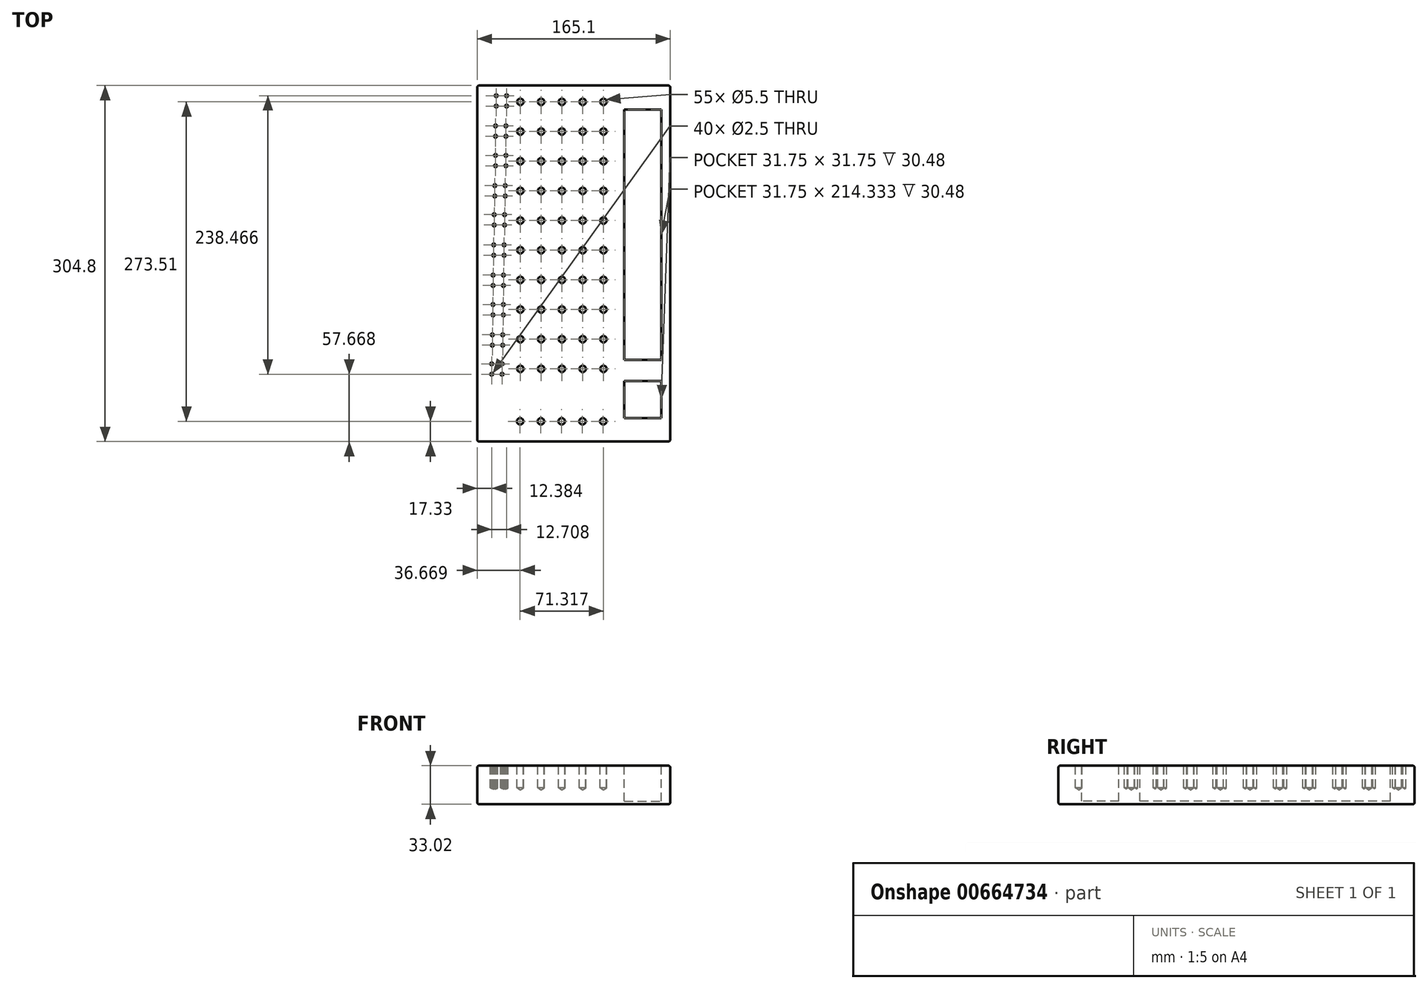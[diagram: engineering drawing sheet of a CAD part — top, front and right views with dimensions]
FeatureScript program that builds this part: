
annotation { "Feature Type Name" : "Feature", "Feature Type Description" : "" }
export const myFeature = defineFeature(function(context is Context, id is Id, definition is map)
    precondition{}
    {
        {
            var Q0;
            Q0=qCreatedBy(makeId("Top.planeOp"),FACE);
            var sketch = newSketch(context, id + "F0", { "sketchPlane" : qUnion([Q0])});
            skLineSegment(sketch, "E0.bottom", {"start": v(-165.1, 224.78) * mm, "end": v(0, 224.78) * mm});
            skLineSegment(sketch, "E0.top", {"start": v(-165.1, -80.02) * mm, "end": v(0, -80.02) * mm});
            skLineSegment(sketch, "E0.left", {"start": v(-165.1, 224.78) * mm, "end": v(-165.1, -80.02) * mm});
            skLineSegment(sketch, "E0.right", {"start": v(0, 224.78) * mm, "end": v(0, -80.02) * mm});
            skSolve(sketch);
        }
        {
            var Q0;
            Q0=makeQuery(id+"F0.imprint","IMPRINT",FACE,{"disambiguationData":[TD([[makeQuery(id+"F0.imprint","IMPRINT",EDGE,{"derivedFrom":sQuery(id+"F0.wireOp",EDGE,"E0.bottom")}),-1.0]])]});
            extrude(context, id + "F1", {"entities" : qUnion([Q0]), "oppositeDirection" : true, "depth" : 33.02 * mm, "offsetDistance" : 25.4 * mm});
        }
        {
            var Q0;
            Q0=makeQuery(id+"F1.opExtrude","SWEPT_FACE",FACE,{"disambiguationData":[OSD([sQuery(id+"F0.wireOp",EDGE,"E0.right")])]});
            var Q1;
            Q1=makeQuery(id+"F1.opExtrude","SWEPT_FACE",FACE,{"disambiguationData":[OSD([sQuery(id+"F0.wireOp",EDGE,"E0.top")])]});
            var Q2;
            Q2=makeQuery(id+"F1.opExtrude","SWEPT_FACE",FACE,{"disambiguationData":[OSD([sQuery(id+"F0.wireOp",EDGE,"E0.left")])]});
            var Q3;
            Q3=makeQuery(id+"F1.opExtrude","SWEPT_FACE",FACE,{"disambiguationData":[OSD([sQuery(id+"F0.wireOp",EDGE,"E0.bottom")])]});
            fillet(context, id + "F2", {"entities" : qUnion([Q0, Q1, Q2, Q3]), "radius" : 1.59 * mm, "tangentPropagation" : true, "allowEdgeOverflow" : false});
        }
        {
            var Q0;
            Q0=makeQuery(id+"F1.opExtrude","CAP_FACE",FACE,{"disambiguationData":[OSD([sQuery(id+"F0.wireOp",EDGE,"E0.bottom"),sQuery(id+"F0.wireOp",EDGE,"E0.top"),sQuery(id+"F0.wireOp",EDGE,"E0.left"),sQuery(id+"F0.wireOp",EDGE,"E0.right")])],"isStart":true});
            var sketch = newSketch(context, id + "F3", { "sketchPlane" : qUnion([Q0])});
            skCircle(sketch, "E1", {"center": v(-128.23, -17.78) * mm, "radius": 2.75 * mm});
            skCircle(sketch, "E2.0.1.0", {"center": v(-128.23, 7.62) * mm, "radius": 2.75 * mm});
            skCircle(sketch, "E2.0.2.0", {"center": v(-128.23, 33.02) * mm, "radius": 2.75 * mm});
            skCircle(sketch, "E2.0.3.0", {"center": v(-128.23, 58.42) * mm, "radius": 2.75 * mm});
            skCircle(sketch, "E2.0.4.0", {"center": v(-128.23, 83.82) * mm, "radius": 2.75 * mm});
            skCircle(sketch, "E2.0.5.0", {"center": v(-128.23, 109.22) * mm, "radius": 2.75 * mm});
            skCircle(sketch, "E2.0.6.0", {"center": v(-128.23, 134.62) * mm, "radius": 2.75 * mm});
            skCircle(sketch, "E2.0.7.0", {"center": v(-128.23, 160.02) * mm, "radius": 2.75 * mm});
            skCircle(sketch, "E2.0.8.0", {"center": v(-128.23, 185.42) * mm, "radius": 2.75 * mm});
            skCircle(sketch, "E2.0.9.0", {"center": v(-128.23, 210.82) * mm, "radius": 2.75 * mm});
            skCircle(sketch, "E2.1.0.0", {"center": v(-110.45, -17.78) * mm, "radius": 2.75 * mm});
            skCircle(sketch, "E2.1.1.0", {"center": v(-110.45, 7.62) * mm, "radius": 2.75 * mm});
            skCircle(sketch, "E2.1.2.0", {"center": v(-110.45, 33.02) * mm, "radius": 2.75 * mm});
            skCircle(sketch, "E2.1.3.0", {"center": v(-110.45, 58.42) * mm, "radius": 2.75 * mm});
            skCircle(sketch, "E2.1.4.0", {"center": v(-110.45, 83.82) * mm, "radius": 2.75 * mm});
            skCircle(sketch, "E2.1.5.0", {"center": v(-110.45, 109.22) * mm, "radius": 2.75 * mm});
            skCircle(sketch, "E2.1.6.0", {"center": v(-110.45, 134.62) * mm, "radius": 2.75 * mm});
            skCircle(sketch, "E2.1.7.0", {"center": v(-110.45, 160.02) * mm, "radius": 2.75 * mm});
            skCircle(sketch, "E2.1.8.0", {"center": v(-110.45, 185.42) * mm, "radius": 2.75 * mm});
            skCircle(sketch, "E2.1.9.0", {"center": v(-110.45, 210.82) * mm, "radius": 2.75 * mm});
            skCircle(sketch, "E2.2.0.0", {"center": v(-92.67, -17.78) * mm, "radius": 2.75 * mm});
            skCircle(sketch, "E2.2.1.0", {"center": v(-92.67, 7.62) * mm, "radius": 2.75 * mm});
            skCircle(sketch, "E2.2.2.0", {"center": v(-92.67, 33.02) * mm, "radius": 2.75 * mm});
            skCircle(sketch, "E2.2.3.0", {"center": v(-92.67, 58.42) * mm, "radius": 2.75 * mm});
            skCircle(sketch, "E2.2.4.0", {"center": v(-92.67, 83.82) * mm, "radius": 2.75 * mm});
            skCircle(sketch, "E2.2.5.0", {"center": v(-92.67, 109.22) * mm, "radius": 2.75 * mm});
            skCircle(sketch, "E2.2.6.0", {"center": v(-92.67, 134.62) * mm, "radius": 2.75 * mm});
            skCircle(sketch, "E2.2.7.0", {"center": v(-92.67, 160.02) * mm, "radius": 2.75 * mm});
            skCircle(sketch, "E2.2.8.0", {"center": v(-92.67, 185.42) * mm, "radius": 2.75 * mm});
            skCircle(sketch, "E2.2.9.0", {"center": v(-92.67, 210.82) * mm, "radius": 2.75 * mm});
            skCircle(sketch, "E2.3.0.0", {"center": v(-74.9, -17.78) * mm, "radius": 2.75 * mm});
            skCircle(sketch, "E2.3.1.0", {"center": v(-74.9, 7.62) * mm, "radius": 2.75 * mm});
            skCircle(sketch, "E2.3.2.0", {"center": v(-74.9, 33.02) * mm, "radius": 2.75 * mm});
            skCircle(sketch, "E2.3.3.0", {"center": v(-74.9, 58.42) * mm, "radius": 2.75 * mm});
            skCircle(sketch, "E2.3.4.0", {"center": v(-74.9, 83.82) * mm, "radius": 2.75 * mm});
            skCircle(sketch, "E2.3.5.0", {"center": v(-74.9, 109.22) * mm, "radius": 2.75 * mm});
            skCircle(sketch, "E2.3.6.0", {"center": v(-74.9, 134.62) * mm, "radius": 2.75 * mm});
            skCircle(sketch, "E2.3.7.0", {"center": v(-74.9, 160.02) * mm, "radius": 2.75 * mm});
            skCircle(sketch, "E2.3.8.0", {"center": v(-74.9, 185.42) * mm, "radius": 2.75 * mm});
            skCircle(sketch, "E2.3.9.0", {"center": v(-74.9, 210.82) * mm, "radius": 2.75 * mm});
            skCircle(sketch, "E2.4.0.0", {"center": v(-57.11, -17.78) * mm, "radius": 2.75 * mm});
            skCircle(sketch, "E2.4.1.0", {"center": v(-57.11, 7.62) * mm, "radius": 2.75 * mm});
            skCircle(sketch, "E2.4.2.0", {"center": v(-57.11, 33.02) * mm, "radius": 2.75 * mm});
            skCircle(sketch, "E2.4.3.0", {"center": v(-57.11, 58.42) * mm, "radius": 2.75 * mm});
            skCircle(sketch, "E2.4.4.0", {"center": v(-57.11, 83.82) * mm, "radius": 2.75 * mm});
            skCircle(sketch, "E2.4.5.0", {"center": v(-57.11, 109.22) * mm, "radius": 2.75 * mm});
            skCircle(sketch, "E2.4.6.0", {"center": v(-57.11, 134.62) * mm, "radius": 2.75 * mm});
            skCircle(sketch, "E2.4.7.0", {"center": v(-57.11, 160.02) * mm, "radius": 2.75 * mm});
            skCircle(sketch, "E2.4.8.0", {"center": v(-57.11, 185.42) * mm, "radius": 2.75 * mm});
            skCircle(sketch, "E2.4.9.0", {"center": v(-57.11, 210.82) * mm, "radius": 2.75 * mm});
            skLineSegment(sketch, "E2.direction1", {"start": v(-128.23, -17.78) * mm, "end": v(-110.45, -17.78) * mm, "construction": true});
            skLineSegment(sketch, "E2.direction2", {"start": v(-128.23, -17.78) * mm, "end": v(-128.23, 7.62) * mm, "construction": true});
            skCircle(sketch, "E3", {"center": v(-148.9, 207.22) * mm, "radius": 1.27 * mm});
            skCircle(sketch, "E4.0.1.0", {"center": v(-148.9, 216.11) * mm, "radius": 1.27 * mm});
            skCircle(sketch, "E4.1.0.0", {"center": v(-140, 207.22) * mm, "radius": 1.27 * mm});
            skCircle(sketch, "E4.1.1.0", {"center": v(-140, 216.11) * mm, "radius": 1.27 * mm});
            skLineSegment(sketch, "E4.direction1", {"start": v(-148.9, 207.22) * mm, "end": v(-140, 207.22) * mm, "construction": true});
            skLineSegment(sketch, "E4.direction2", {"start": v(-148.9, 207.22) * mm, "end": v(-148.9, 216.11) * mm, "construction": true});
            skCircle(sketch, "E5", {"center": v(-149.45, 181.36) * mm, "radius": 1.27 * mm});
            skCircle(sketch, "E6.0.1.0", {"center": v(-149.45, 190.25) * mm, "radius": 1.27 * mm});
            skCircle(sketch, "E6.1.0.0", {"center": v(-140.56, 181.36) * mm, "radius": 1.27 * mm});
            skCircle(sketch, "E6.1.1.0", {"center": v(-140.56, 190.25) * mm, "radius": 1.27 * mm});
            skLineSegment(sketch, "E6.direction1", {"start": v(-149.45, 181.36) * mm, "end": v(-140.56, 181.36) * mm, "construction": true});
            skLineSegment(sketch, "E6.direction2", {"start": v(-149.45, 181.36) * mm, "end": v(-149.45, 190.25) * mm, "construction": true});
            skCircle(sketch, "E7", {"center": v(-149.51, 156.12) * mm, "radius": 1.27 * mm});
            skCircle(sketch, "E8.0.1.0", {"center": v(-149.51, 165) * mm, "radius": 1.27 * mm});
            skCircle(sketch, "E8.1.0.0", {"center": v(-140.62, 156.12) * mm, "radius": 1.27 * mm});
            skCircle(sketch, "E8.1.1.0", {"center": v(-140.62, 165) * mm, "radius": 1.27 * mm});
            skLineSegment(sketch, "E8.direction1", {"start": v(-149.51, 156.12) * mm, "end": v(-140.62, 156.12) * mm, "construction": true});
            skLineSegment(sketch, "E8.direction2", {"start": v(-149.51, 156.12) * mm, "end": v(-149.51, 165) * mm, "construction": true});
            skCircle(sketch, "E9", {"center": v(-150.07, 130.25) * mm, "radius": 1.27 * mm});
            skCircle(sketch, "E10.0.1.0", {"center": v(-150.07, 139.14) * mm, "radius": 1.27 * mm});
            skCircle(sketch, "E10.1.0.0", {"center": v(-141.18, 130.25) * mm, "radius": 1.27 * mm});
            skCircle(sketch, "E10.1.1.0", {"center": v(-141.18, 139.14) * mm, "radius": 1.27 * mm});
            skLineSegment(sketch, "E10.direction1", {"start": v(-150.07, 130.25) * mm, "end": v(-141.18, 130.25) * mm, "construction": true});
            skLineSegment(sketch, "E10.direction2", {"start": v(-150.07, 130.25) * mm, "end": v(-150.07, 139.14) * mm, "construction": true});
            skCircle(sketch, "E11", {"center": v(-150.58, 105.4) * mm, "radius": 1.27 * mm});
            skCircle(sketch, "E12.0.1.0", {"center": v(-150.58, 114.3) * mm, "radius": 1.27 * mm});
            skCircle(sketch, "E12.1.0.0", {"center": v(-141.69, 105.4) * mm, "radius": 1.27 * mm});
            skCircle(sketch, "E12.1.1.0", {"center": v(-141.69, 114.3) * mm, "radius": 1.27 * mm});
            skLineSegment(sketch, "E12.direction1", {"start": v(-150.58, 105.4) * mm, "end": v(-141.69, 105.4) * mm, "construction": true});
            skLineSegment(sketch, "E12.direction2", {"start": v(-150.58, 105.4) * mm, "end": v(-150.58, 114.3) * mm, "construction": true});
            skCircle(sketch, "E13", {"center": v(-151.04, 79.47) * mm, "radius": 1.27 * mm});
            skCircle(sketch, "E14.0.1.0", {"center": v(-151.04, 88.36) * mm, "radius": 1.27 * mm});
            skCircle(sketch, "E14.1.0.0", {"center": v(-142.15, 79.47) * mm, "radius": 1.27 * mm});
            skCircle(sketch, "E14.1.1.0", {"center": v(-142.15, 88.36) * mm, "radius": 1.27 * mm});
            skLineSegment(sketch, "E14.direction1", {"start": v(-151.04, 79.47) * mm, "end": v(-142.15, 79.47) * mm, "construction": true});
            skLineSegment(sketch, "E14.direction2", {"start": v(-151.04, 79.47) * mm, "end": v(-151.04, 88.36) * mm, "construction": true});
            skCircle(sketch, "E15", {"center": v(-151.6, 53.6) * mm, "radius": 1.27 * mm});
            skCircle(sketch, "E16.0.1.0", {"center": v(-151.6, 62.5) * mm, "radius": 1.27 * mm});
            skCircle(sketch, "E16.1.0.0", {"center": v(-142.7, 53.6) * mm, "radius": 1.27 * mm});
            skCircle(sketch, "E16.1.1.0", {"center": v(-142.7, 62.5) * mm, "radius": 1.27 * mm});
            skLineSegment(sketch, "E16.direction1", {"start": v(-151.6, 53.6) * mm, "end": v(-142.7, 53.6) * mm, "construction": true});
            skLineSegment(sketch, "E16.direction2", {"start": v(-151.6, 53.6) * mm, "end": v(-151.6, 62.5) * mm, "construction": true});
            skCircle(sketch, "E17", {"center": v(-151.65, 28.36) * mm, "radius": 1.27 * mm});
            skCircle(sketch, "E18.0.1.0", {"center": v(-151.65, 37.25) * mm, "radius": 1.27 * mm});
            skCircle(sketch, "E18.1.0.0", {"center": v(-142.76, 28.36) * mm, "radius": 1.27 * mm});
            skCircle(sketch, "E18.1.1.0", {"center": v(-142.76, 37.25) * mm, "radius": 1.27 * mm});
            skLineSegment(sketch, "E18.direction1", {"start": v(-151.65, 28.36) * mm, "end": v(-142.76, 28.36) * mm, "construction": true});
            skLineSegment(sketch, "E18.direction2", {"start": v(-151.65, 28.36) * mm, "end": v(-151.65, 37.25) * mm, "construction": true});
            skCircle(sketch, "E19", {"center": v(-152.2, 2.5) * mm, "radius": 1.27 * mm});
            skCircle(sketch, "E20.0.1.0", {"center": v(-152.2, 11.39) * mm, "radius": 1.27 * mm});
            skCircle(sketch, "E20.1.0.0", {"center": v(-143.32, 2.5) * mm, "radius": 1.27 * mm});
            skCircle(sketch, "E20.1.1.0", {"center": v(-143.32, 11.39) * mm, "radius": 1.27 * mm});
            skLineSegment(sketch, "E20.direction1", {"start": v(-152.2, 2.5) * mm, "end": v(-143.32, 2.5) * mm, "construction": true});
            skLineSegment(sketch, "E20.direction2", {"start": v(-152.2, 2.5) * mm, "end": v(-152.2, 11.39) * mm, "construction": true});
            skCircle(sketch, "E21", {"center": v(-152.72, -22.35) * mm, "radius": 1.27 * mm});
            skCircle(sketch, "E22.0.1.0", {"center": v(-152.72, -13.46) * mm, "radius": 1.27 * mm});
            skCircle(sketch, "E22.1.0.0", {"center": v(-143.83, -22.35) * mm, "radius": 1.27 * mm});
            skCircle(sketch, "E22.1.1.0", {"center": v(-143.83, -13.46) * mm, "radius": 1.27 * mm});
            skLineSegment(sketch, "E22.direction1", {"start": v(-152.72, -22.35) * mm, "end": v(-143.83, -22.35) * mm, "construction": true});
            skLineSegment(sketch, "E22.direction2", {"start": v(-152.72, -22.35) * mm, "end": v(-152.72, -13.46) * mm, "construction": true});
            skSolve(sketch);
        }
        {
            var Q0;
            Q0=sQuery(id+"F3.wireOp",VERTEX,"E2.2.8.0.center");
            var Q1;
            Q1=sQuery(id+"F3.wireOp",VERTEX,"E2.2.2.0.center");
            var Q2;
            Q2=sQuery(id+"F3.wireOp",VERTEX,"E2.4.9.0.center");
            var Q3;
            Q3=sQuery(id+"F3.wireOp",VERTEX,"E2.3.3.0.center");
            var Q4;
            Q4=sQuery(id+"F3.wireOp",VERTEX,"E2.4.0.0.center");
            var Q5;
            Q5=sQuery(id+"F3.wireOp",VERTEX,"E2.0.6.0.center");
            var Q6;
            Q6=sQuery(id+"F3.wireOp",VERTEX,"E2.2.1.0.center");
            var Q7;
            Q7=sQuery(id+"F3.wireOp",VERTEX,"E2.4.7.0.center");
            var Q8;
            Q8=sQuery(id+"F3.wireOp",VERTEX,"E2.3.1.0.center");
            var Q9;
            Q9=sQuery(id+"F3.wireOp",VERTEX,"E2.1.5.0.center");
            var Q10;
            Q10=sQuery(id+"F3.wireOp",VERTEX,"E2.0.5.0.center");
            var Q11;
            Q11=sQuery(id+"F3.wireOp",VERTEX,"E2.0.4.0.center");
            var Q12;
            Q12=sQuery(id+"F3.wireOp",VERTEX,"E2.2.0.0.center");
            var Q13;
            Q13=sQuery(id+"F3.wireOp",VERTEX,"E2.1.1.0.center");
            var Q14;
            Q14=sQuery(id+"F3.wireOp",VERTEX,"E2.3.8.0.center");
            var Q15;
            Q15=sQuery(id+"F3.wireOp",VERTEX,"E2.4.6.0.center");
            var Q16;
            Q16=sQuery(id+"F3.wireOp",VERTEX,"E2.2.7.0.center");
            var Q17;
            Q17=sQuery(id+"F3.wireOp",VERTEX,"E2.3.7.0.center");
            var Q18;
            Q18=sQuery(id+"F3.wireOp",VERTEX,"E2.4.3.0.center");
            var Q19;
            Q19=sQuery(id+"F3.wireOp",VERTEX,"E2.3.0.0.center");
            var Q20;
            Q20=sQuery(id+"F3.wireOp",VERTEX,"E2.1.4.0.center");
            var Q21;
            Q21=sQuery(id+"F3.wireOp",VERTEX,"E2.1.2.0.center");
            var Q22;
            Q22=sQuery(id+"F3.wireOp",VERTEX,"E2.2.4.0.center");
            var Q23;
            Q23=sQuery(id+"F3.wireOp",VERTEX,"E2.1.7.0.center");
            var Q24;
            Q24=sQuery(id+"F3.wireOp",VERTEX,"E2.0.1.0.center");
            var Q25;
            Q25=sQuery(id+"F3.wireOp",VERTEX,"E2.0.8.0.center");
            var Q26;
            Q26=sQuery(id+"F3.wireOp",VERTEX,"E2.3.9.0.center");
            var Q27;
            Q27=sQuery(id+"F3.wireOp",VERTEX,"E2.0.7.0.center");
            var Q28;
            Q28=sQuery(id+"F3.wireOp",VERTEX,"E2.4.4.0.center");
            var Q29;
            Q29=sQuery(id+"F3.wireOp",VERTEX,"E2.2.3.0.center");
            var Q30;
            Q30=sQuery(id+"F3.wireOp",VERTEX,"E2.direction2.start");
            var Q31;
            Q31=sQuery(id+"F3.wireOp",VERTEX,"E2.direction1.end");
            var Q32;
            Q32=sQuery(id+"F3.wireOp",VERTEX,"E2.1.3.0.center");
            var Q33;
            Q33=sQuery(id+"F3.wireOp",VERTEX,"E2.2.9.0.center");
            var Q34;
            Q34=sQuery(id+"F3.wireOp",VERTEX,"E2.4.5.0.center");
            var Q35;
            Q35=sQuery(id+"F3.wireOp",VERTEX,"E2.3.6.0.center");
            var Q36;
            Q36=sQuery(id+"F3.wireOp",VERTEX,"E2.4.2.0.center");
            var Q37;
            Q37=sQuery(id+"F3.wireOp",VERTEX,"E2.3.5.0.center");
            var Q38;
            Q38=sQuery(id+"F3.wireOp",VERTEX,"E2.0.3.0.center");
            var Q39;
            Q39=sQuery(id+"F3.wireOp",VERTEX,"E2.1.9.0.center");
            var Q40;
            Q40=sQuery(id+"F3.wireOp",VERTEX,"E2.2.6.0.center");
            var Q41;
            Q41=sQuery(id+"F3.wireOp",VERTEX,"E2.1.6.0.center");
            var Q42;
            Q42=sQuery(id+"F3.wireOp",VERTEX,"E2.3.2.0.center");
            var Q43;
            Q43=sQuery(id+"F3.wireOp",VERTEX,"E2.4.8.0.center");
            var Q44;
            Q44=sQuery(id+"F3.wireOp",VERTEX,"E2.3.4.0.center");
            var Q45;
            Q45=sQuery(id+"F3.wireOp",VERTEX,"E2.4.1.0.center");
            var Q46;
            Q46=sQuery(id+"F3.wireOp",VERTEX,"E2.0.2.0.center");
            var Q47;
            Q47=sQuery(id+"F3.wireOp",VERTEX,"E2.0.9.0.center");
            var Q48;
            Q48=sQuery(id+"F3.wireOp",VERTEX,"E2.1.8.0.center");
            var Q49;
            Q49=sQuery(id+"F3.wireOp",VERTEX,"E2.2.5.0.center");
            var Q50;
            Q50=makeQuery(id+"F1.opExtrude","SWEPT_BODY",BODY,{"disambiguationData":[OSD([sQuery(id+"F0.wireOp",EDGE,"E0.bottom"),sQuery(id+"F0.wireOp",EDGE,"E0.top"),sQuery(id+"F0.wireOp",EDGE,"E0.left"),sQuery(id+"F0.wireOp",EDGE,"E0.right")])]});
            hole(context, id + "F4", {"style" : HoleStyle.SIMPLE, "endStyle" : HoleEndStyle.BLIND, "holeDiameter" : 5.5 * mm, "majorDiameter" : 6.35 * mm, "holeDepth" : 19.05 * mm, "isTappedThrough" : true, "tappedDepth" : 12.7 * mm, "tapClearance" : 3, "locations" : qUnion([Q0, Q1, Q2, Q3, Q4, Q5, Q6, Q7, Q8, Q9, Q10, Q11, Q12, Q13, Q14, Q15, Q16, Q17, Q18, Q19, Q20, Q21, Q22, Q23, Q24, Q25, Q26, Q27, Q28, Q29, Q30, Q31, Q32, Q33, Q34, Q35, Q36, Q37, Q38, Q39, Q40, Q41, Q42, Q43, Q44, Q45, Q46, Q47, Q48, Q49]), "scope" : qUnion([Q50])});
        }
        {
            var Q0;
            Q0=sQuery(id+"F3.wireOp",VERTEX,"E12.direction2.end");
            var Q1;
            Q1=sQuery(id+"F3.wireOp",VERTEX,"E18.1.1.0.center");
            var Q2;
            Q2=sQuery(id+"F3.wireOp",VERTEX,"E14.1.0.0.center");
            var Q3;
            Q3=sQuery(id+"F3.wireOp",VERTEX,"E10.1.1.0.center");
            var Q4;
            Q4=sQuery(id+"F3.wireOp",VERTEX,"E22.1.0.0.center");
            var Q5;
            Q5=sQuery(id+"F3.wireOp",VERTEX,"E6.1.0.0.center");
            var Q6;
            Q6=sQuery(id+"F3.wireOp",VERTEX,"E22.direction2.start");
            var Q7;
            Q7=sQuery(id+"F3.wireOp",VERTEX,"E14.direction2.start");
            var Q8;
            Q8=sQuery(id+"F3.wireOp",VERTEX,"E9.center");
            var Q9;
            Q9=sQuery(id+"F3.wireOp",VERTEX,"E22.direction2.end");
            var Q10;
            Q10=sQuery(id+"F3.wireOp",VERTEX,"E14.direction2.end");
            var Q11;
            Q11=sQuery(id+"F3.wireOp",VERTEX,"E10.0.1.0.center");
            var Q12;
            Q12=sQuery(id+"F3.wireOp",VERTEX,"E18.direction1.end");
            var Q13;
            Q13=sQuery(id+"F3.wireOp",VERTEX,"E18.0.1.0.center");
            var Q14;
            Q14=sQuery(id+"F3.wireOp",VERTEX,"E12.1.0.0.center");
            var Q15;
            Q15=sQuery(id+"F3.wireOp",VERTEX,"E16.0.1.0.center");
            var Q16;
            Q16=sQuery(id+"F3.wireOp",VERTEX,"E10.direction1.end");
            var Q17;
            Q17=sQuery(id+"F3.wireOp",VERTEX,"E4.1.1.0.center");
            var Q18;
            Q18=sQuery(id+"F3.wireOp",VERTEX,"E12.1.1.0.center");
            var Q19;
            Q19=sQuery(id+"F3.wireOp",VERTEX,"E20.1.1.0.center");
            var Q20;
            Q20=sQuery(id+"F3.wireOp",VERTEX,"E20.1.0.0.center");
            var Q21;
            Q21=sQuery(id+"F3.wireOp",VERTEX,"E17.center");
            var Q22;
            Q22=sQuery(id+"F3.wireOp",VERTEX,"E16.direction1.end");
            var Q23;
            Q23=sQuery(id+"F3.wireOp",VERTEX,"E12.direction1.start");
            var Q24;
            Q24=sQuery(id+"F3.wireOp",VERTEX,"E20.direction1.start");
            var Q25;
            Q25=sQuery(id+"F3.wireOp",VERTEX,"E8.direction1.start");
            var Q26;
            Q26=sQuery(id+"F3.wireOp",VERTEX,"E6.direction2.end");
            var Q27;
            Q27=sQuery(id+"F3.wireOp",VERTEX,"E6.direction2.start");
            var Q28;
            Q28=sQuery(id+"F3.wireOp",VERTEX,"E4.direction2.end");
            var Q29;
            Q29=sQuery(id+"F3.wireOp",VERTEX,"E4.direction2.start");
            var Q30;
            Q30=sQuery(id+"F3.wireOp",VERTEX,"E4.direction1.end");
            var Q31;
            Q31=sQuery(id+"F3.wireOp",VERTEX,"E20.direction2.end");
            var Q32;
            Q32=sQuery(id+"F3.wireOp",VERTEX,"E16.1.1.0.center");
            var Q33;
            Q33=sQuery(id+"F3.wireOp",VERTEX,"E8.direction2.end");
            var Q34;
            Q34=sQuery(id+"F3.wireOp",VERTEX,"E8.1.1.0.center");
            var Q35;
            Q35=sQuery(id+"F3.wireOp",VERTEX,"E8.direction1.end");
            var Q36;
            Q36=sQuery(id+"F3.wireOp",VERTEX,"E15.center");
            var Q37;
            Q37=sQuery(id+"F3.wireOp",VERTEX,"E6.1.1.0.center");
            var Q38;
            Q38=sQuery(id+"F3.wireOp",VERTEX,"E14.1.1.0.center");
            var Q39;
            Q39=sQuery(id+"F3.wireOp",VERTEX,"E22.1.1.0.center");
            var Q40;
            Q40=makeQuery(id+"F1.opExtrude","SWEPT_BODY",BODY,{"disambiguationData":[OSD([sQuery(id+"F0.wireOp",EDGE,"E0.bottom"),sQuery(id+"F0.wireOp",EDGE,"E0.top"),sQuery(id+"F0.wireOp",EDGE,"E0.left"),sQuery(id+"F0.wireOp",EDGE,"E0.right")])]});
            hole(context, id + "F5", {"style" : HoleStyle.SIMPLE, "endStyle" : HoleEndStyle.BLIND, "holeDiameter" : 2.5 * mm, "majorDiameter" : 6.35 * mm, "holeDepth" : 19.05 * mm, "isTappedThrough" : true, "tappedDepth" : 12.7 * mm, "tapClearance" : 3, "locations" : qUnion([Q0, Q1, Q2, Q3, Q4, Q5, Q6, Q7, Q8, Q9, Q10, Q11, Q12, Q13, Q14, Q15, Q16, Q17, Q18, Q19, Q20, Q21, Q22, Q23, Q24, Q25, Q26, Q27, Q28, Q29, Q30, Q31, Q32, Q33, Q34, Q35, Q36, Q37, Q38, Q39]), "scope" : qUnion([Q40])});
        }
        {
            var Q0;
            Q0=makeQuery(id+"F3.imprint","IMPRINT",FACE,{"disambiguationData":[TD([[makeQuery(id+"F3.imprint","IMPRINT",EDGE,{"derivedFrom":sQuery(id+"F3.wireOp",EDGE,"E1")}),-1.0]])]});
            var sketch = newSketch(context, id + "F6", { "sketchPlane" : qUnion([Q0])});
            skCircle(sketch, "E23", {"center": v(-128.43, -62.69) * mm, "radius": 2.75 * mm});
            skCircle(sketch, "E24.1.0.0", {"center": v(-110.65, -62.69) * mm, "radius": 2.75 * mm});
            skCircle(sketch, "E24.2.0.0", {"center": v(-92.87, -62.69) * mm, "radius": 2.75 * mm});
            skCircle(sketch, "E24.3.0.0", {"center": v(-75.1, -62.69) * mm, "radius": 2.75 * mm});
            skCircle(sketch, "E24.4.0.0", {"center": v(-57.31, -62.69) * mm, "radius": 2.75 * mm});
            skLineSegment(sketch, "E24.direction1", {"start": v(-128.43, -62.69) * mm, "end": v(-110.65, -62.69) * mm, "construction": true});
            skSolve(sketch);
        }
        {
            var Q0;
            Q0=sQuery(id+"F6.wireOp",VERTEX,"E24.4.0.0.center");
            var Q1;
            Q1=sQuery(id+"F6.wireOp",VERTEX,"E24.direction1.start");
            var Q2;
            Q2=sQuery(id+"F6.wireOp",VERTEX,"E24.3.0.0.center");
            var Q3;
            Q3=sQuery(id+"F6.wireOp",VERTEX,"E24.1.0.0.center");
            var Q4;
            Q4=sQuery(id+"F6.wireOp",VERTEX,"E24.2.0.0.center");
            var Q5;
            Q5=makeQuery(id+"F1.opExtrude","SWEPT_BODY",BODY,{"disambiguationData":[OSD([sQuery(id+"F0.wireOp",EDGE,"E0.bottom"),sQuery(id+"F0.wireOp",EDGE,"E0.top"),sQuery(id+"F0.wireOp",EDGE,"E0.left"),sQuery(id+"F0.wireOp",EDGE,"E0.right")])]});
            hole(context, id + "F7", {"style" : HoleStyle.SIMPLE, "endStyle" : HoleEndStyle.BLIND, "holeDiameter" : 5.5 * mm, "majorDiameter" : 6.35 * mm, "holeDepth" : 19.05 * mm, "isTappedThrough" : true, "tappedDepth" : 12.7 * mm, "tapClearance" : 3, "locations" : qUnion([Q0, Q1, Q2, Q3, Q4]), "scope" : qUnion([Q5])});
        }
        {
            var Q0;
            Q0=makeQuery(id+"F3.imprint","IMPRINT",FACE,{"disambiguationData":[TD([[makeQuery(id+"F3.imprint","IMPRINT",EDGE,{"derivedFrom":sQuery(id+"F3.wireOp",EDGE,"E1")}),-1.0]])]});
            var sketch = newSketch(context, id + "F8", { "sketchPlane" : qUnion([Q0])});
            skLineSegment(sketch, "E25.bottom", {"start": v(-39.37, 204.17) * mm, "end": v(-7.62, 204.17) * mm});
            skLineSegment(sketch, "E25.top", {"start": v(-39.37, -10.16) * mm, "end": v(-7.62, -10.16) * mm});
            skLineSegment(sketch, "E25.left", {"start": v(-39.37, 204.17) * mm, "end": v(-39.37, -10.16) * mm});
            skLineSegment(sketch, "E25.right", {"start": v(-7.62, 204.17) * mm, "end": v(-7.62, -10.16) * mm});
            skLineSegment(sketch, "E26.bottom", {"start": v(-39.38, -28.22) * mm, "end": v(-7.63, -28.22) * mm});
            skLineSegment(sketch, "E26.top", {"start": v(-39.38, -59.97) * mm, "end": v(-7.63, -59.97) * mm});
            skLineSegment(sketch, "E26.left", {"start": v(-39.38, -28.22) * mm, "end": v(-39.38, -59.97) * mm});
            skLineSegment(sketch, "E26.right", {"start": v(-7.63, -28.22) * mm, "end": v(-7.63, -59.97) * mm});
            skSolve(sketch);
        }
        {
            var Q0;
            Q0=makeQuery(id+"F8.imprint","IMPRINT",FACE,{"disambiguationData":[TD([[makeQuery(id+"F8.imprint","IMPRINT",EDGE,{"derivedFrom":sQuery(id+"F8.wireOp",EDGE,"E25.bottom")}),-1.0]])]});
            var Q1;
            Q1=makeQuery(id+"F8.imprint","IMPRINT",FACE,{"disambiguationData":[TD([[makeQuery(id+"F8.imprint","IMPRINT",EDGE,{"derivedFrom":sQuery(id+"F8.wireOp",EDGE,"E26.bottom")}),-1.0]])]});
            extrude(context, id + "F9", {"entities" : qUnion([Q0, Q1]), "operationType" : NewBodyOperationType.REMOVE, "oppositeDirection" : true, "depth" : 30.48 * mm, "offsetDistance" : 25.4 * mm});
        }
    });
